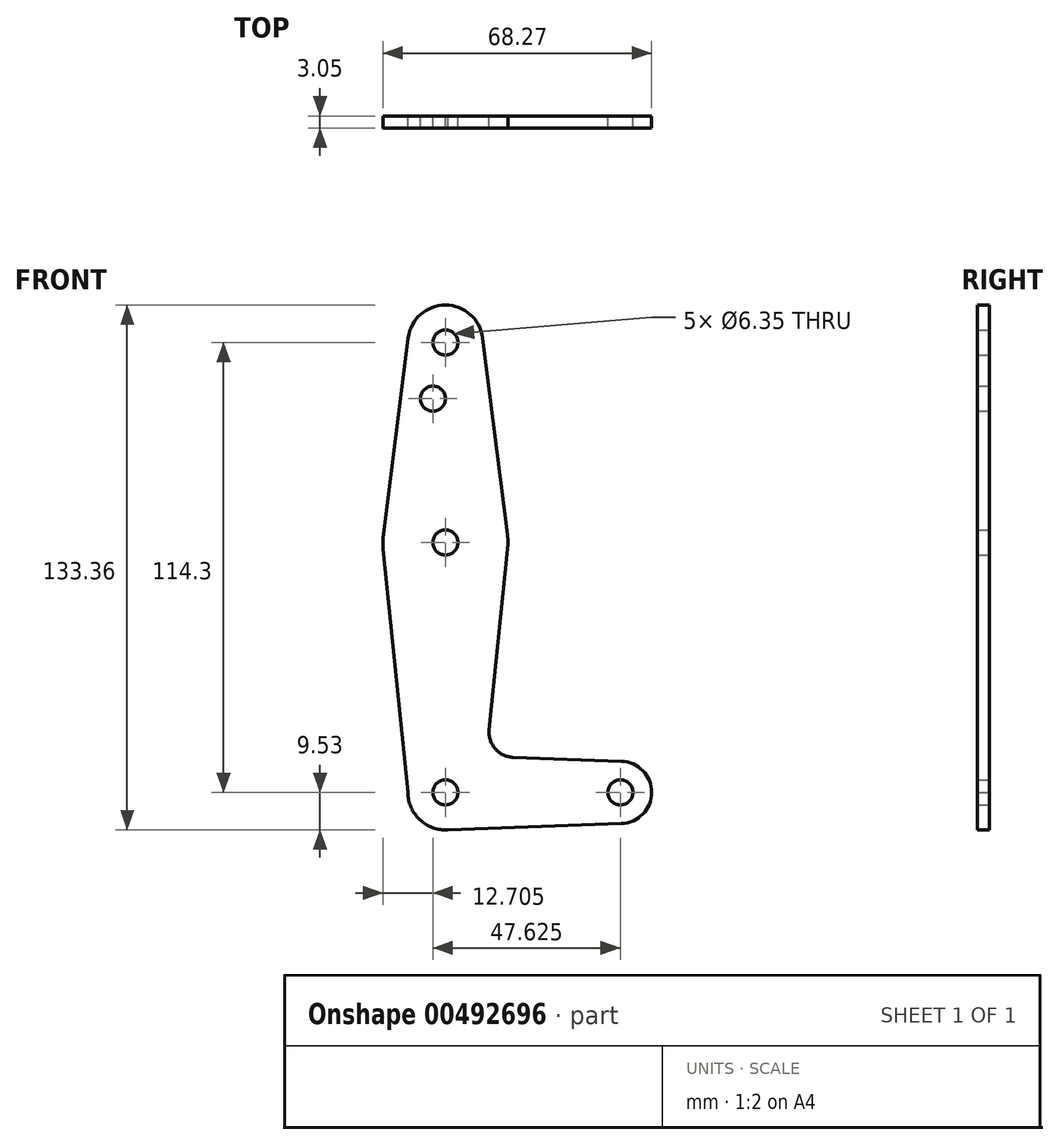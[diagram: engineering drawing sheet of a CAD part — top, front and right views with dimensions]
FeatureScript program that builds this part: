
annotation { "Feature Type Name" : "Feature", "Feature Type Description" : "" }
export const myFeature = defineFeature(function(context is Context, id is Id, definition is map)
    precondition{}
    {
        {
            var Q0;
            Q0=qCreatedBy(makeId("Front.planeOp"),FACE);
            var sketch = newSketch(context, id + "F0", { "sketchPlane" : qUnion([Q0])});
            skLineSegment(sketch, "E0", {"start": v(0, 114.3) * mm, "end": v(0, 114.3) * mm});
            skLineSegment(sketch, "E1", {"start": v(0, 114.3) * mm, "end": v(0, 0) * mm});
            skLineSegment(sketch, "E2", {"start": v(0, 0) * mm, "end": v(44.45, 0) * mm});
            skCircle(sketch, "E3", {"center": v(0, 114.3) * mm, "radius": 9.53 * mm});
            skCircle(sketch, "E4", {"center": v(0, 0) * mm, "radius": 9.53 * mm});
            skCircle(sketch, "E5", {"center": v(44.45, 0) * mm, "radius": 7.94 * mm});
            skCircle(sketch, "E6", {"center": v(0, 63.5) * mm, "radius": 15.88 * mm});
            skLineSegment(sketch, "E7", {"start": v(17.23, 8.91) * mm, "end": v(44.73, 7.93) * mm});
            skLineSegment(sketch, "E8", {"start": v(0, -9.52) * mm, "end": v(44.73, -7.93) * mm});
            skLineSegment(sketch, "E9", {"start": v(-9.45, 115.5) * mm, "end": v(-15.75, 65.48) * mm});
            skLineSegment(sketch, "E10", {"start": v(-9.52, 0) * mm, "end": v(-15.8, 61.9) * mm});
            skLineSegment(sketch, "E11", {"start": v(11.14, 15.9) * mm, "end": v(15.8, 61.9) * mm});
            skLineSegment(sketch, "E12", {"start": v(9.45, 115.5) * mm, "end": v(15.75, 65.48) * mm});
            skCircle(sketch, "E13", {"center": v(0, 114.3) * mm, "radius": 3.18 * mm});
            skCircle(sketch, "E14", {"center": v(0, 63.5) * mm, "radius": 3.18 * mm});
            skCircle(sketch, "E15", {"center": v(0, 0) * mm, "radius": 3.18 * mm});
            skCircle(sketch, "E16", {"center": v(44.45, 0) * mm, "radius": 3.18 * mm});
            skCircle(sketch, "E17", {"center": v(-3.17, 100.03) * mm, "radius": 3.18 * mm});
            skPoint(sketch, "E18.newPointB", {"position": v(0, 9.53) * mm});
            skArc(sketch, "E18.filletArc", {"start": v(11.14, 15.9) * mm, "mid": v(12.67, 11.08) * mm, "end": v(17.23, 8.91) * mm});
            skSolve(sketch);
        }
        {
            var Q0;
            Q0 = qSketchRegion(id + "F0", true);
            var Q1;
            {var subQ0=sQuery(id+"F0.wireOp",EDGE,"E4");var subQ1=sQuery(id+"F0.wireOp",EDGE,"E1");var subQ2=makeQuery(id+"F0.imprint","INTERSECT",VERTEX,{"derivedFrom":[subQ1,subQ0]});Q1=makeQuery(id+"F0.imprint","IMPRINT",FACE,{"disambiguationData":[TD([[makeQuery(id+"F0.imprint","IMPRINT",EDGE,{"disambiguationData":[TD([[subQ2,-1.0]])],"derivedFrom":subQ1}),1.0]])]});}
            extrude(context, id + "F1", {"entities" : qUnion([Q0, Q1]), "depth" : 3.05 * mm});
        }
    });
